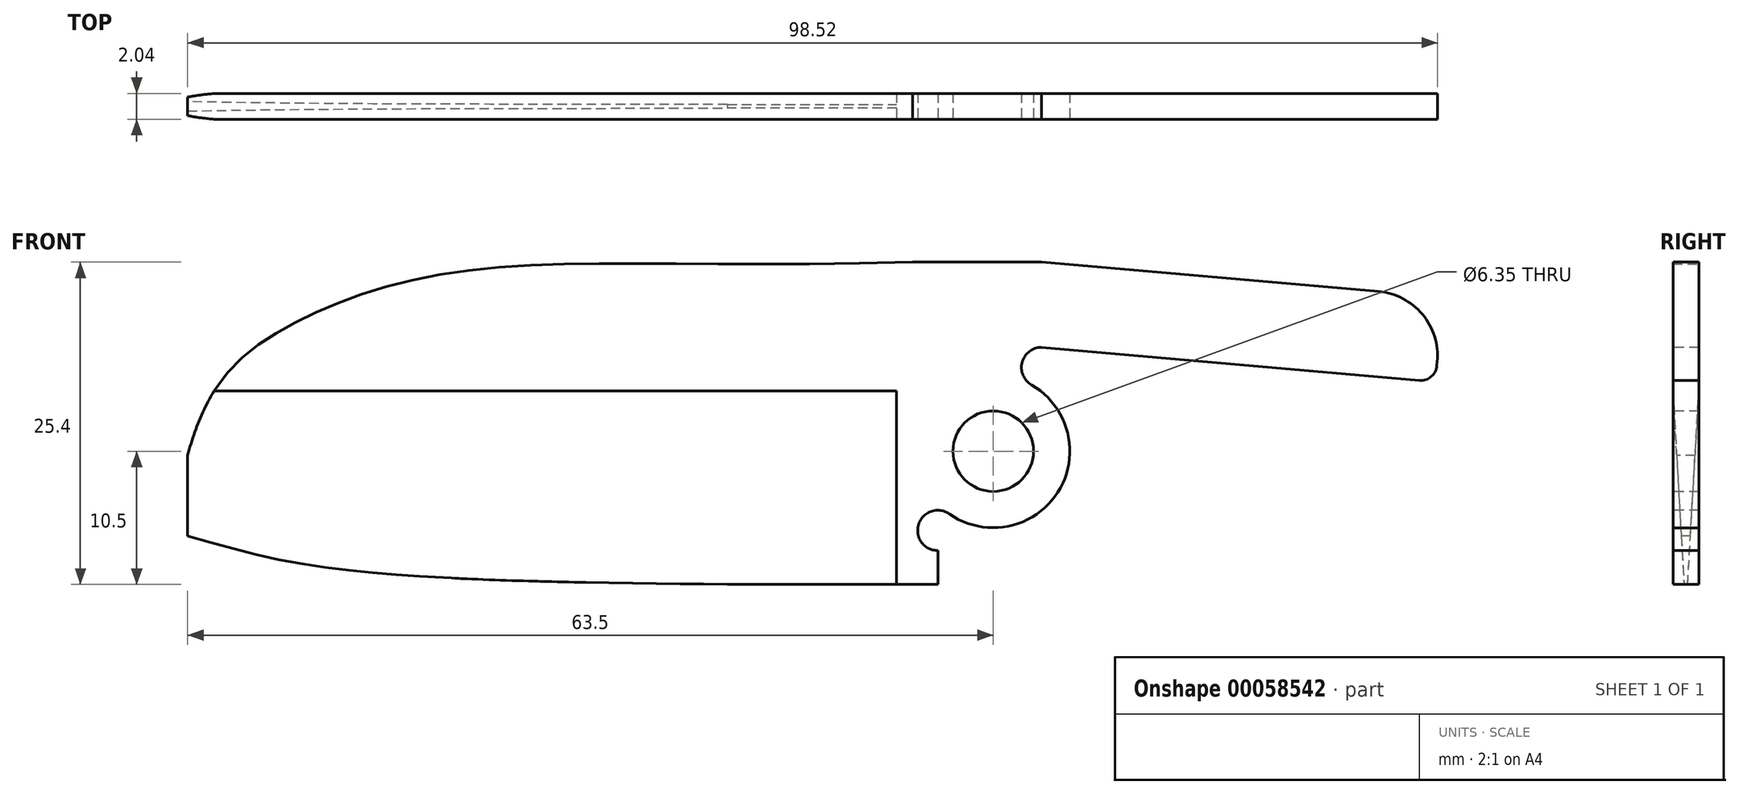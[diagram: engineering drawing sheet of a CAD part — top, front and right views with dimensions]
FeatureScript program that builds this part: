
annotation { "Feature Type Name" : "Feature", "Feature Type Description" : "" }
export const myFeature = defineFeature(function(context is Context, id is Id, definition is map)
    precondition{}
    {
        {
            var Q0;
            Q0=qCreatedBy(makeId("Front.planeOp"),FACE);
            var sketch = newSketch(context, id + "F0", { "sketchPlane" : qUnion([Q0])});
            skCircle(sketch, "E0", {"center": v(0, 0) * mm, "radius": 3.18 * mm});
            skCircle(sketch, "E1", {"center": v(3.81, 6.6) * mm, "radius": 1.59 * mm});
            skCircle(sketch, "E2", {"center": v(-4.37, -6.24) * mm, "radius": 1.59 * mm});
            skLineSegment(sketch, "E3", {"start": v(3.81, 6.6) * mm, "end": v(0, 0) * mm, "construction": true});
            skLineSegment(sketch, "E4", {"start": v(0, 0) * mm, "end": v(-4.37, -6.24) * mm, "construction": true});
            skArc(sketch, "E5", {"start": v(4.6, 7.97) * mm, "mid": v(7.77, -4.95) * mm, "end": v(-5.28, -7.54) * mm, "construction": true});
            skArc(sketch, "E6", {"start": v(3.02, 5.22) * mm, "mid": v(5.09, -3.24) * mm, "end": v(-3.46, -4.94) * mm, "construction": true});
            skSolve(sketch);
        }
        {
            var Q0;
            Q0=qCreatedBy(makeId("Front.planeOp"),FACE);
            var sketch = newSketch(context, id + "F1", { "sketchPlane" : qUnion([Q0])});
            skLineSegment(sketch, "E7.bottom", {"start": v(-63.5, -10.5) * mm, "end": v(10.48, -10.5) * mm});
            skLineSegment(sketch, "E7.top", {"start": v(-63.5, 14.9) * mm, "end": v(10.48, 14.9) * mm});
            skLineSegment(sketch, "E7.left", {"start": v(-63.5, -10.5) * mm, "end": v(-63.5, 14.9) * mm});
            skLineSegment(sketch, "E7.right", {"start": v(10.48, -10.5) * mm, "end": v(10.48, 14.9) * mm});
            skLineSegment(sketch, "E8", {"start": v(-7.35, -10.5) * mm, "end": v(-4.37, -6.24) * mm, "construction": true});
            skPoint(sketch, "E9.start.orphan", {"position": v(3.8, 6.6) * mm});
            skLineSegment(sketch, "E10", {"start": v(8.6, 14.9) * mm, "end": v(4.6, 7.97) * mm, "construction": true});
            skLineSegment(sketch, "E11", {"start": v(5.4, 6.6) * mm, "end": v(10.48, 6.6) * mm, "construction": true});
            skSolve(sketch);
        }
        {
            var Q0;
            Q0=makeQuery(id+"F1.imprint","IMPRINT",FACE,{"disambiguationData":[TD([[makeQuery(id+"F1.imprint","IMPRINT",EDGE,{"derivedFrom":sQuery(id+"F1.wireOp",EDGE,"E7.bottom")}),1.0]])]});
            extrude(context, id + "F2", {"entities" : qUnion([Q0]), "endBound" : BoundingType.SYMMETRIC, "depth" : 2.03 * mm});
        }
        {
            var Q0;
            Q0=qSketchRegion(id+"F0",true);
            extrude(context, id + "F3", {"entities" : qUnion([Q0]), "operationType" : NewBodyOperationType.REMOVE, "endBound" : BoundingType.SYMMETRIC, "oppositeDirection" : true, "depth" : 25.4 * mm});
        }
        {
            var Q0;
            Q0=qCreatedBy(makeId("Front.planeOp"),FACE);
            var sketch = newSketch(context, id + "F4", { "sketchPlane" : qUnion([Q0])});
            skLineSegment(sketch, "E12", {"start": v(3.8, 14.9) * mm, "end": v(3.81, 6.6) * mm});
            skLineSegment(sketch, "E13", {"start": v(-4.37, -6.24) * mm, "end": v(-4.37, -10.5) * mm});
            skLineSegment(sketch, "E14", {"start": v(-4.37, -10.5) * mm, "end": v(10.48, -10.5) * mm});
            skLineSegment(sketch, "E15", {"start": v(10.48, -10.5) * mm, "end": v(10.48, 14.9) * mm});
            skLineSegment(sketch, "E16", {"start": v(10.48, 14.9) * mm, "end": v(3.8, 14.9) * mm});
            skArc(sketch, "E17", {"start": v(3.02, 5.22) * mm, "mid": v(5.09, -3.24) * mm, "end": v(-3.46, -4.94) * mm});
            skLineSegment(sketch, "E18", {"start": v(3.02, 5.22) * mm, "end": v(3.81, 6.6) * mm});
            skLineSegment(sketch, "E19", {"start": v(-4.37, -6.24) * mm, "end": v(-3.46, -4.94) * mm});
            skSolve(sketch);
        }
        {
            var Q0;
            Q0=qSketchRegion(id+"F4",true);
            extrude(context, id + "F5", {"entities" : qUnion([Q0]), "operationType" : NewBodyOperationType.REMOVE, "endBound" : BoundingType.SYMMETRIC, "oppositeDirection" : true, "depth" : 25.4 * mm});
        }
        {
            var Q0;
            Q0=makeQuery(id+"F2.opExtrude","CAP_FACE",FACE,{"disambiguationData":[OSD([sQuery(id+"F1.wireOp",EDGE,"E7.bottom"),sQuery(id+"F1.wireOp",EDGE,"E7.top"),sQuery(id+"F1.wireOp",EDGE,"E7.left"),sQuery(id+"F1.wireOp",EDGE,"E7.right")])],"isStart":false});
            var sketch = newSketch(context, id + "F6", { "sketchPlane" : qUnion([Q0])});
            skFitSpline(sketch, "E20", {"points": [v(-63.5, -0.34) * mm, v(-56.26, 9.44) * mm, v(-42.55, 14.1) * mm, v(-6.35, 14.9) * mm], "startDerivative": vector(17.5, 64.7) * mm, "endDerivative": vector(110, 3.37) * mm});
            skLineSegment(sketch, "E21", {"start": v(-63.5, -0.34) * mm, "end": v(-63.5, 14.9) * mm});
            skLineSegment(sketch, "E22", {"start": v(-63.5, 14.9) * mm, "end": v(-6.35, 14.9) * mm});
            skSolve(sketch);
        }
        {
            var Q0;
            Q0=qSketchRegion(id+"F6",true);
            extrude(context, id + "F7", {"entities" : qUnion([Q0]), "operationType" : NewBodyOperationType.REMOVE, "oppositeDirection" : true, "depth" : 25.4 * mm});
        }
        {
            var Q0;
            Q0=makeQuery(id+"F2.opExtrude","CAP_FACE",FACE,{"disambiguationData":[OSD([sQuery(id+"F1.wireOp",EDGE,"E7.bottom"),sQuery(id+"F1.wireOp",EDGE,"E7.top"),sQuery(id+"F1.wireOp",EDGE,"E7.left"),sQuery(id+"F1.wireOp",EDGE,"E7.right")])],"isStart":false});
            var sketch = newSketch(context, id + "F8", { "sketchPlane" : qUnion([Q0])});
            skFitSpline(sketch, "E23", {"points": [v(-63.5, -6.69) * mm, v(-52.2, -9.23) * mm, v(-20.95, -10.5) * mm], "startDerivative": vector(29.07, -8.13) * mm, "endDerivative": vector(56.26, -0.61) * mm});
            skLineSegment(sketch, "E24", {"start": v(-63.5, -6.69) * mm, "end": v(-63.5, -10.5) * mm});
            skLineSegment(sketch, "E25", {"start": v(-63.5, -10.5) * mm, "end": v(-20.95, -10.5) * mm});
            skSolve(sketch);
        }
        {
            var Q0;
            Q0=qSketchRegion(id+"F8",true);
            extrude(context, id + "F9", {"entities" : qUnion([Q0]), "operationType" : NewBodyOperationType.REMOVE, "oppositeDirection" : true, "depth" : 25.4 * mm});
        }
        {
            var Q0;
            Q0=makeQuery(id+"F2.opExtrude","CAP_FACE",FACE,{"disambiguationData":[OSD([sQuery(id+"F1.wireOp",EDGE,"E7.bottom"),sQuery(id+"F1.wireOp",EDGE,"E7.top"),sQuery(id+"F1.wireOp",EDGE,"E7.left"),sQuery(id+"F1.wireOp",EDGE,"E7.right")])],"isStart":false});
            var sketch = newSketch(context, id + "F10", { "sketchPlane" : qUnion([Q0])});
            skLineSegment(sketch, "E26", {"start": v(3.81, 14.9) * mm, "end": v(35.44, 12.14) * mm});
            skLineSegment(sketch, "E27", {"start": v(35.44, 12.14) * mm, "end": v(34.86, 5.47) * mm});
            skLineSegment(sketch, "E28", {"start": v(34.86, 5.47) * mm, "end": v(3.8, 8.19) * mm});
            skLineSegment(sketch, "E29", {"start": v(3.8, 8.19) * mm, "end": v(3.8, 14.9) * mm});
            skSolve(sketch);
        }
        {
            var Q0;
            Q0=qSketchRegion(id+"F10",true);
            var Q1;
            Q1=makeQuery(id+"F2.opExtrude","CAP_FACE",FACE,{"disambiguationData":[OSD([sQuery(id+"F1.wireOp",EDGE,"E7.bottom"),sQuery(id+"F1.wireOp",EDGE,"E7.top"),sQuery(id+"F1.wireOp",EDGE,"E7.left"),sQuery(id+"F1.wireOp",EDGE,"E7.right")])],"isStart":true});
            extrude(context, id + "F11", {"entities" : qUnion([Q0]), "operationType" : NewBodyOperationType.ADD, "endBound" : BoundingType.UP_TO_SURFACE, "oppositeDirection" : true, "endBoundEntityFace" : qUnion([Q1]), "depth" : 2.54 * mm});
        }
        {
            var Q0;
            Q0=makeQuery(id+"F11.opExtrude","SWEPT_EDGE",EDGE,{"disambiguationData":[OSD([sQuery(id+"F10.wireOp",EDGE,"E26"),sQuery(id+"F10.wireOp",EDGE,"E27")])]});
            fillet(context, id + "F12", {"entities" : qUnion([Q0]), "radius" : 5.08 * mm, "tangentPropagation" : true, "allowEdgeOverflow" : false});
        }
        {
            var Q0;
            Q0=makeQuery(id+"F11.opExtrude","SWEPT_EDGE",EDGE,{"disambiguationData":[OSD([sQuery(id+"F10.wireOp",EDGE,"E27"),sQuery(id+"F10.wireOp",EDGE,"E28")])]});
            fillet(context, id + "F13", {"entities" : qUnion([Q0]), "radius" : 1.27 * mm, "tangentPropagation" : true, "allowEdgeOverflow" : false});
        }
        {
            var Q0;
            Q0=makeQuery(id+"F2.opExtrude","SWEPT_FACE",FACE,{"disambiguationData":[OSD([sQuery(id+"F1.wireOp",EDGE,"E7.left")])]});
            var sketch = newSketch(context, id + "F14", { "sketchPlane" : qUnion([Q0])});
            skLineSegment(sketch, "E30", {"start": v(-1.02, 4.74) * mm, "end": v(-1.02, -13.04) * mm});
            skLineSegment(sketch, "E31", {"start": v(-1.02, -13.04) * mm, "end": v(0, -13.04) * mm});
            skLineSegment(sketch, "E32", {"start": v(0, -13.04) * mm, "end": v(-1.02, 4.74) * mm});
            skLineSegment(sketch, "E33", {"start": v(0, -13.04) * mm, "end": v(1.02, -13.04) * mm});
            skLineSegment(sketch, "E34", {"start": v(1.02, -13.04) * mm, "end": v(1.02, 4.74) * mm});
            skLineSegment(sketch, "E35", {"start": v(1.02, 4.74) * mm, "end": v(0, -13.04) * mm});
            skSolve(sketch);
        }
        {
            var Q0;
            Q0=qSketchRegion(id+"F14",true);
            extrude(context, id + "F15", {"entities" : qUnion([Q0]), "operationType" : NewBodyOperationType.REMOVE, "oppositeDirection" : true, "depth" : 55.88 * mm});
        }
    });
